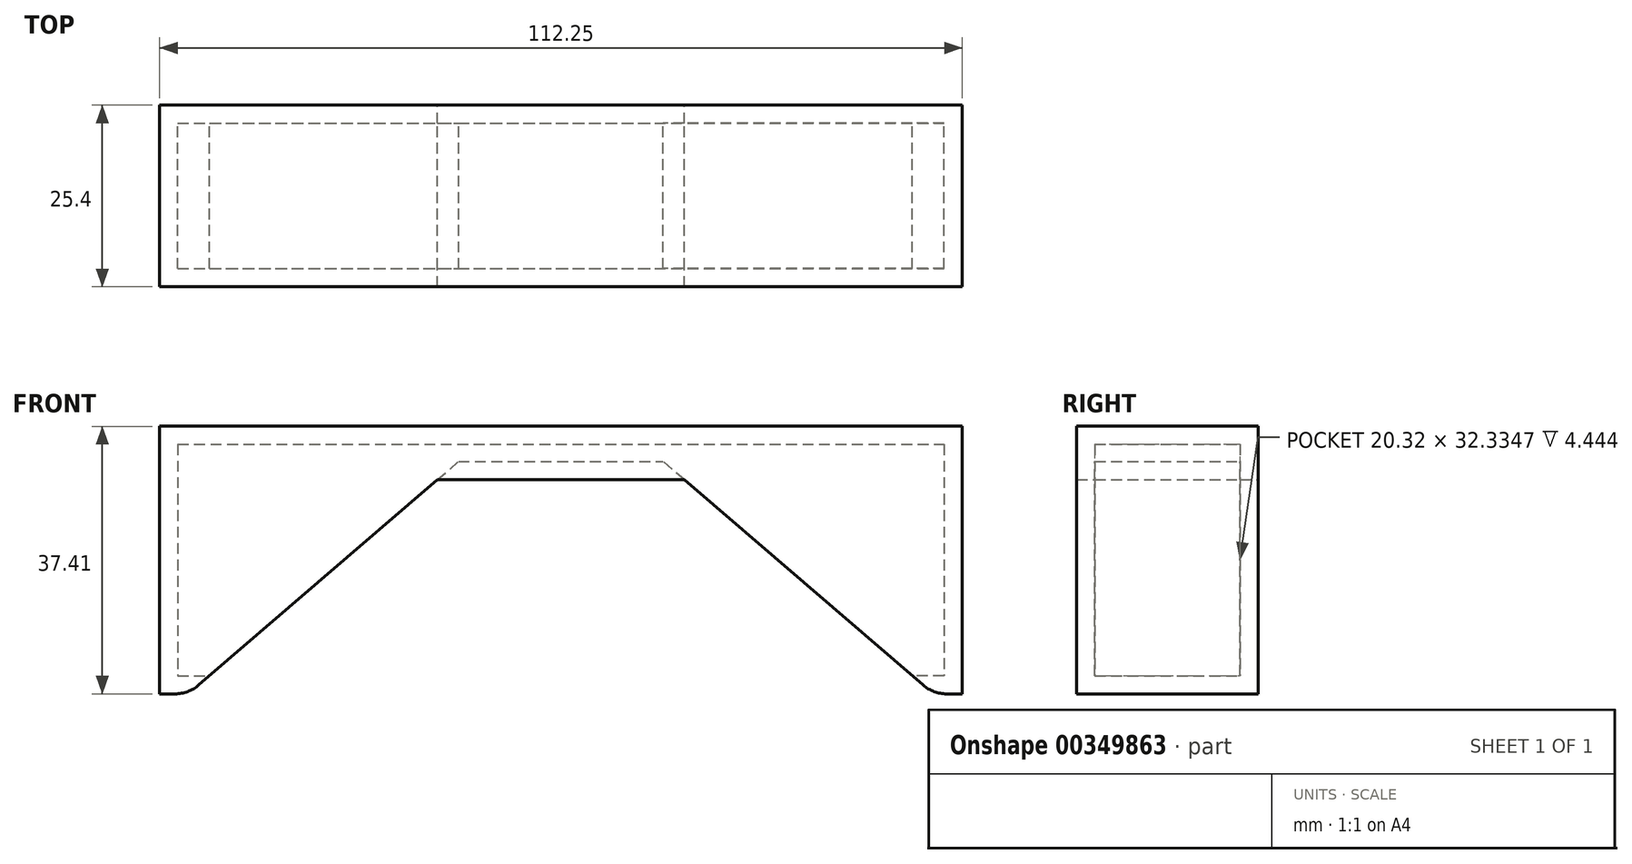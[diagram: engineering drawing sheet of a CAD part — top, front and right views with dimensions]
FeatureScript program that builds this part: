
annotation { "Feature Type Name" : "Feature", "Feature Type Description" : "" }
export const myFeature = defineFeature(function(context is Context, id is Id, definition is map)
    precondition{}
    {
        {
            var Q0;
            Q0=qCreatedBy(makeId("Front.planeOp"),FACE);
            var sketch = newSketch(context, id + "F0", { "sketchPlane" : qUnion([Q0])});
            skLineSegment(sketch, "E0", {"start": v(-57.85, 37.41) * mm, "end": v(54.4, 37.41) * mm});
            skLineSegment(sketch, "E1", {"start": v(-57.85, 37.41) * mm, "end": v(-57.85, 29.93) * mm});
            skLineSegment(sketch, "E2", {"start": v(-57.85, 29.93) * mm, "end": v(54.4, 29.93) * mm});
            skLineSegment(sketch, "E3", {"start": v(54.4, 29.93) * mm, "end": v(54.4, 37.41) * mm});
            skLineSegment(sketch, "E4", {"start": v(-57.85, 29.93) * mm, "end": v(-57.85, 0) * mm});
            skLineSegment(sketch, "E5", {"start": v(-57.85, 0) * mm, "end": v(-53.82, 0) * mm});
            skLineSegment(sketch, "E6", {"start": v(-53.82, 0) * mm, "end": v(-53.82, 29.93) * mm});
            skLineSegment(sketch, "E7", {"start": v(54.4, 29.93) * mm, "end": v(54.4, 0) * mm});
            skLineSegment(sketch, "E8", {"start": v(54.4, 0) * mm, "end": v(50.37, 0) * mm});
            skLineSegment(sketch, "E9", {"start": v(50.37, 0) * mm, "end": v(50.37, 29.93) * mm});
            skLineSegment(sketch, "E10", {"start": v(-53.82, 0) * mm, "end": v(-19, 29.93) * mm});
            skLineSegment(sketch, "E11", {"start": v(50.37, 0) * mm, "end": v(15.54, 29.93) * mm});
            skSolve(sketch);
        }
        {
            var Q0;
            {var subQ0=sQuery(id+"F0.wireOp",EDGE,"E6");Q0=makeQuery(id+"F0.imprint","IMPRINT",FACE,{"disambiguationData":[TD([[makeQuery(id+"F0.imprint","IMPRINT",EDGE,{"derivedFrom":subQ0}),-1.0]])]});}
            extrude(context, id + "F1", {"entities" : qUnion([Q0]), "depth" : 25.4 * mm});
        }
        {
            var Q0;
            Q0 = qSketchRegion(id + "F0", true);
            extrude(context, id + "F2", {"entities" : qUnion([Q0]), "operationType" : NewBodyOperationType.ADD, "depth" : 25.4 * mm});
        }
        {
            var Q0;
            Q0=makeQuery(id+"F1.opExtrude","SWEPT_FACE",FACE,{"disambiguationData":[OSD([sQuery(id+"F0.wireOp",EDGE,"E10")])]});
            var Q1;
            Q1=makeQuery(id+"F2.opExtrude","SWEPT_FACE",FACE,{"disambiguationData":[OSD([sQuery(id+"F0.wireOp",EDGE,"E11")])]});
            shell(context, id + "F3", {"entities" : qUnion([Q0, Q1]), "thickness" : 2.54 * mm});
        }
        {
            var Q0;
            {var subQ0=sQuery(id+"F0.wireOp",EDGE,"E10");var subQ1=sQuery(id+"F0.wireOp",EDGE,"E6");var subQ2=sQuery(id+"F0.wireOp",EDGE,"E5");Q0=makeQuery(id+"F2.boolean.opBoolean","MERGE",EDGE,{"derivedFrom":[makeQuery(id+"F1.opExtrude","SWEPT_EDGE",EDGE,{"disambiguationData":[OSD([subQ2,subQ1,subQ0])]}),makeQuery(id+"F2.opExtrude","SWEPT_EDGE",EDGE,{"disambiguationData":[OSD([subQ2,subQ1,subQ0])]})]});}
            fillet(context, id + "F4", {"entities" : qUnion([Q0]), "radius" : 5.08 * mm, "tangentPropagation" : true, "allowEdgeOverflow" : false});
        }
        {
            var Q0;
            Q0=makeQuery(id+"F2.opExtrude","SWEPT_EDGE",EDGE,{"disambiguationData":[OSD([sQuery(id+"F0.wireOp",EDGE,"E8"),sQuery(id+"F0.wireOp",EDGE,"E9"),sQuery(id+"F0.wireOp",EDGE,"E11")])]});
            fillet(context, id + "F5", {"entities" : qUnion([Q0]), "radius" : 5.08 * mm, "tangentPropagation" : true, "allowEdgeOverflow" : false});
        }
    });
